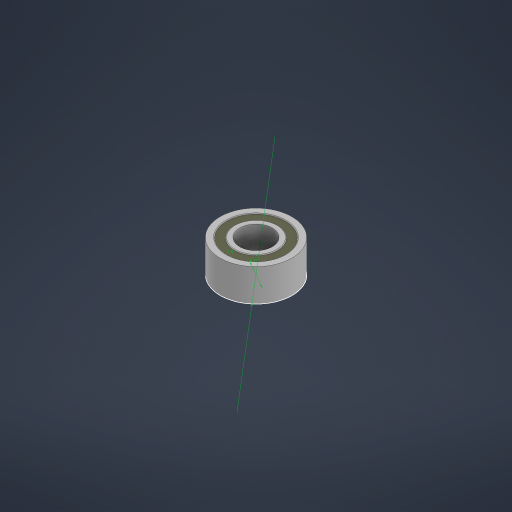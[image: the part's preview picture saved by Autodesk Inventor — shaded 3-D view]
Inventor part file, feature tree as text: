
AUTODESK INVENTOR PART (.ipt)
format: ipt  version: 2024 (Build 280153000, 153)  size: 228,864 bytes
history: native  units: mm
features: extrude x3, sketch x1, fillet x1
ambient origin geometry x8: Origin, YZ Plane, XZ Plane, XY Plane, X Axis, Y Axis, Z Axis, Center Point
bodies: Solid1 (feature_tree)
feature tree (5):
  sketch  "Sketch1"  dims[d0=11.0mm d1=5.0mm d2=0.9mm d3=0.7mm d4=4.95mm d5=0.0mm d6=0.1mm d7=0.0mm d8=0.1mm d9=0.0mm d10=0.1mm]
  extrude  "Extrusion1"  Depth=0.1mm
  extrude  "Extrusion2"  Depth=0.1mm
  extrude  "Extrusion3"  Depth=0.1mm
  fillet  "Fillet1"  Radius=4.95mm
